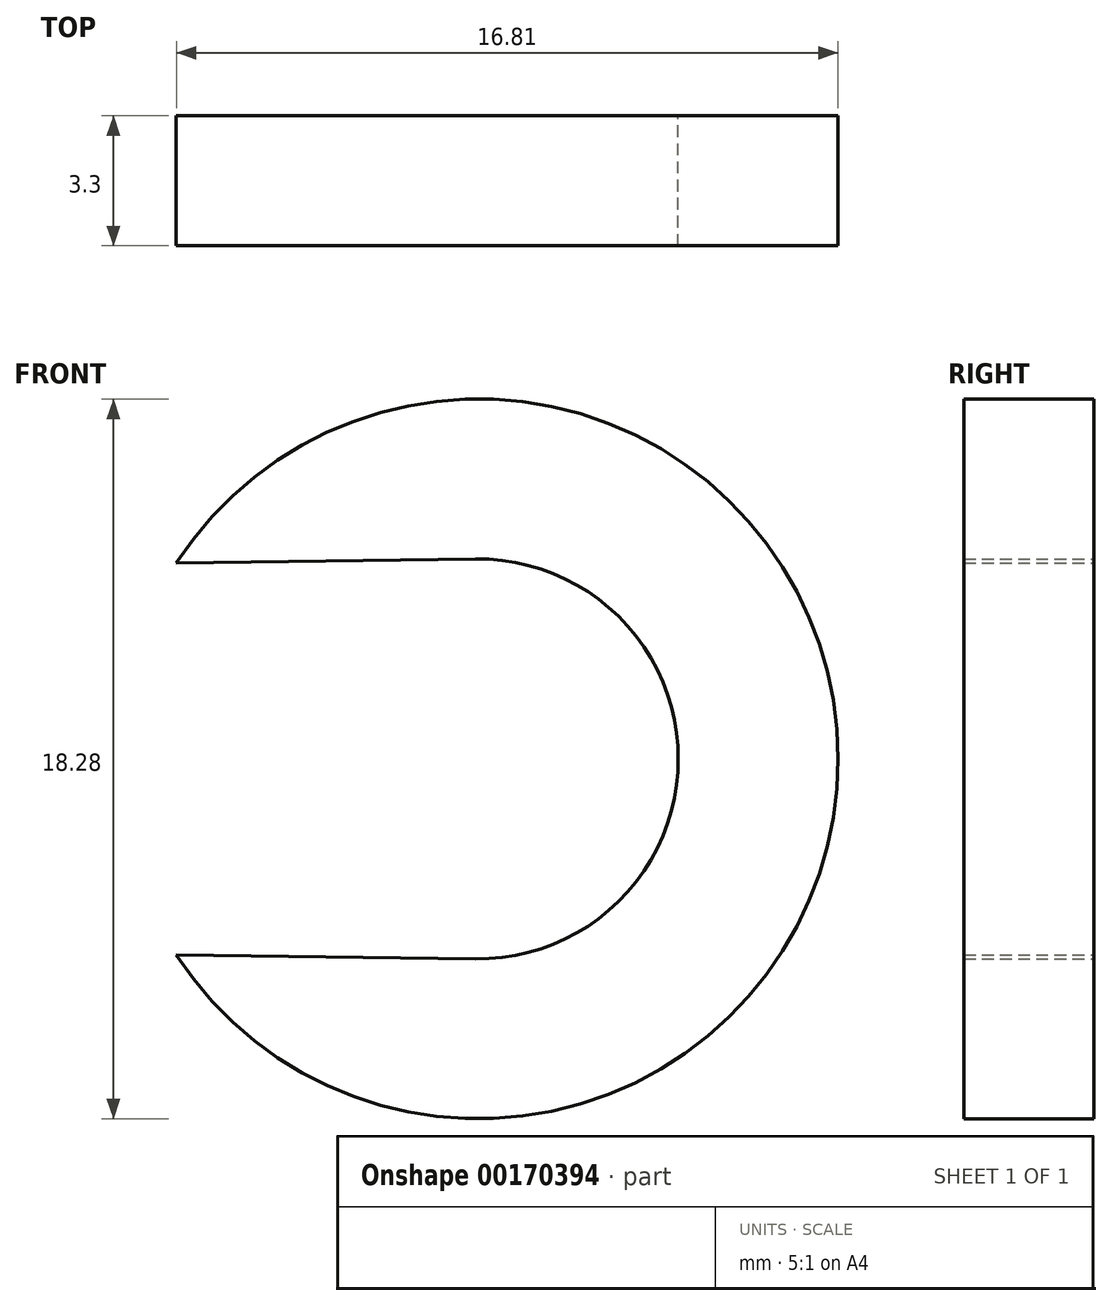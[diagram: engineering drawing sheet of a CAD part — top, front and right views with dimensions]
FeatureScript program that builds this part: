
annotation { "Feature Type Name" : "Feature", "Feature Type Description" : "" }
export const myFeature = defineFeature(function(context is Context, id is Id, definition is map)
    precondition{}
    {
        {
            var Q0;
            Q0=qCreatedBy(makeId("Front.planeOp"),FACE);
            var sketch = newSketch(context, id + "F0", { "sketchPlane" : qUnion([Q0])});
            skArc(sketch, "E0", {"start": v(-7.67, -4.97) * mm, "mid": v(9.14, 0) * mm, "end": v(-7.67, 4.97) * mm});
            skArc(sketch, "E1", {"start": v(-0.07, -5.08) * mm, "mid": v(5.08, 0) * mm, "end": v(-0.07, 5.08) * mm});
            skLineSegment(sketch, "E2", {"start": v(-9.14, 0) * mm, "end": v(-9.14, 4.95) * mm, "construction": true});
            skLineSegment(sketch, "E3", {"start": v(-9.14, 0) * mm, "end": v(-9.14, -4.95) * mm, "construction": true});
            skLineSegment(sketch, "E4", {"start": v(-7.67, 4.97) * mm, "end": v(0, 5.08) * mm});
            skLineSegment(sketch, "E5", {"start": v(-7.67, -4.97) * mm, "end": v(0, -5.08) * mm});
            skSolve(sketch);
        }
        {
            var Q0;
            Q0 = qSketchRegion(id + "F0", true);
            extrude(context, id + "F1", {"entities" : qUnion([Q0]), "depth" : 3.3 * mm});
        }
    });
